# Revit family: Krome C9021-C9028 VS seris
name_source: partatom
category: Pipe Fittings
revit_build: Autodesk Revit 2018 (Build: 20170223_1515(x64)
units: mm (PartAtom-declared; Revit-internal decimal feet)

## family parameters
Always vertical = Yes
Cut with Voids When Loaded = No
Part Type = Elbow
Round Connector Dimension = Use Diameter
Shared = No
Work Plane-Based = No

## types (8) — shared parameters
Model = C9021 - VS Series
URL = https://kromedispense.co.in

## per-type parameters (varying)
| type | Weight (kgs) |
| C9022-VS-16"  Balance Grab Bar Vibrant Stainless | .79 |
| C9021-VS-12"  Balance Grab Bar Vibrant Stainless | 0.71 |
| C9026-VS-36"  Balance Grab Bar Vibrant Stainless | 1.18 |
| C9024-VS-24"  Balance Grab Bar Vibrant Stainless | .94 |
| C9023-VS-18"  Balance Grab Bar Vibrant Stainless | 0.83 |
| C9028-VS-48"  Balance Grab Bar Vibrant Stainless | 1.42 |
| C9027-VS-42"  Balance Grab Bar Vibrant Stainless | 1.3 |
| C9025-VS-30"  Balance Grab Bar Vibrant Stainless | 1.06 |

## geometry (parser evidence)
native form markers: Sweep x3
no freeform markers — native parametric forms only
